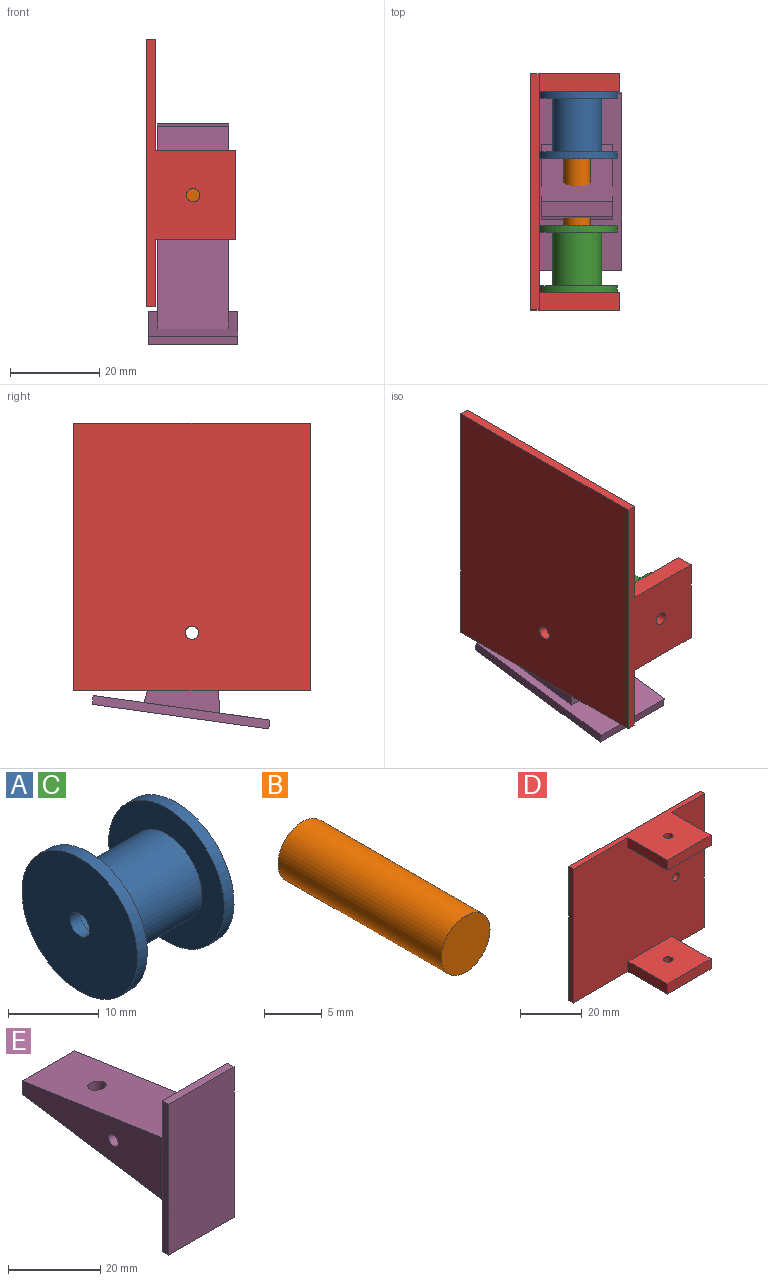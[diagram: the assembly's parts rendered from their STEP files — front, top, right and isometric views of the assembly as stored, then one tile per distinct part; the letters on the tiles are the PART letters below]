
ASSEMBLY  parts=5 mates=4
PART A: 10 faces, bbox 15x18x18 mm
  f0: plane 18x18mm, normal (-1,0,0), area 247.4mm2, adj f1,f9
  f1: cylinder r=1.5mm len=3mm, axis (-1,0,0), area 14.1mm2, adj f0,f2
  f2: plane 9x9mm, normal (1,0,0), area 56.5mm2, adj f1,f3
  f3: cylinder r=4.5mm len=13.5mm, axis (-1,0,0), area 381.7mm2, adj f2,f4
  f4: plane 18x18mm, normal (1,0,0), area 190.9mm2, adj f3,f5
  f5: cylinder r=9mm len=18mm, axis (-1,0,0), area 84.8mm2, adj f4,f6
  f6: plane 18x18mm, normal (-1,0,0), area 159.4mm2, adj f5,f7
  f7: cylinder r=5.5mm len=12mm, axis (-1,0,0), area 414.7mm2, adj f6,f8
  f8: plane 18x18mm, normal (1,0,0), area 159.4mm2, adj f7,f9
  f9: cylinder r=9mm len=18mm, axis (-1,0,0), area 84.8mm2, adj f0,f8
PART B: 3 faces, bbox 6x20x6 mm
  f0: cylinder r=3mm len=20mm, axis (0,1,0), area 377mm2, adj f1,f2
  f1: plane 6x6mm, normal (0,-1,0), area 28.3mm2, adj f0
  f2: plane 6x6mm, normal (0,1,0), area 28.3mm2, adj f0
PART C: same geometry as A
PART D: 17 faces, bbox 60x20x53 mm
  f0: plane 60x53mm, normal (0,-1,0), area 3012.9mm2, adj f1,f2,f3,f4,f6,f7,f8,f9
  f1: plane 60x20mm, normal (0,0,-1), area 472.9mm2, adj f0,f2,f4,f5,f12,f13,f14,f15
  f2: plane 53x2mm, normal (1,0,0), area 106mm2, adj f0,f1,f3,f5
  f3: plane 60x20mm, normal (0,0,1), area 472.9mm2, adj f0,f2,f4,f5,f7,f9,f10,f16
  f4: plane 53x2mm, normal (-1,0,0), area 106mm2, adj f0,f1,f3,f5
  f5: plane 60x53mm, normal (0,1,0), area 3172.9mm2, adj f1,f2,f3,f4,f6
  f6: cylinder r=1.5mm len=3mm, axis (0,-1,0), area 18.8mm2, adj f0,f5
  f7: plane 18x4mm, normal (-1,0,0), area 72mm2, adj f0,f3,f8,f10
  f8: plane 20x18mm, normal (0,0,-1), area 352.9mm2, adj f0,f7,f9,f10,f16
  f9: plane 18x4mm, normal (1,0,0), area 72mm2, adj f0,f3,f8,f10
  f10: plane 20x4mm, normal (0,-1,0), area 80mm2, adj f3,f7,f8,f9
  f11: plane 20x18mm, normal (0,0,1), area 352.9mm2, adj f0,f12,f13,f14,f15
  f12: plane 18x4mm, normal (-1,0,0), area 72mm2, adj f0,f1,f11,f14
  f13: plane 18x4mm, normal (1,0,0), area 72mm2, adj f0,f1,f11,f14
  f14: plane 20x4mm, normal (0,-1,0), area 80mm2, adj f1,f11,f12,f13
  f15: cylinder r=1.5mm len=4mm, axis (0,0,1), area 37.7mm2, adj f1,f11
  f16: cylinder r=1.5mm len=4mm, axis (0,0,1), area 37.7mm2, adj f3,f8
PART E: 13 faces, bbox 20.1x47.1x40.1 mm
  f0: plane 40x20mm, normal (0,1,0), area 528mm2, adj f1,f2,f3,f4,f6,f8,f9,f10
  f1: plane 20x2mm, normal (0,0,-1), area 40mm2, adj f0,f2,f4,f5
  f2: plane 40x2mm, normal (1,0,0), area 80mm2, adj f0,f1,f3,f5
  f3: plane 20x2mm, normal (0,0,1), area 40mm2, adj f0,f2,f4,f5
  f4: plane 40x2mm, normal (-1,0,0), area 80mm2, adj f0,f1,f3,f5
  f5: plane 40x20mm, normal (0,-1,0), area 800mm2, adj f1,f2,f3,f4
  f6: plane 45x16mm, normal (0,0.15,-0.99), area 715.3mm2, adj f0,f7,f9,f10,f12
  f7: plane 16x3.55mm, normal (0,1,0), area 56.8mm2, adj f6,f8,f9,f10
  f8: plane 45.13x16.13mm, normal (0,0.15,0.99), area 715.3mm2, adj f0,f7,f9,f10,f12
  f9: plane 45x17mm, normal (1,0,0), area 455.3mm2, adj f0,f6,f7,f8,f11
  f10: plane 45x17mm, normal (-1,0,0), area 455.3mm2, adj f0,f6,f7,f8,f11
  f11: cylinder r=1.5mm len=16mm, axis (-1,0,0), area 150.8mm2, adj f9,f10
  f12: cylinder r=2mm len=8.63mm, axis (0,0,-1), area 100.9mm2, adj f6,f8
PLACE A rot(axis=(0.71,-0.71,0),180deg) t=(-4.45,76.44,-45.22)mm
PLACE B rot(axis=(1,0,0),7.9deg) t=(-4.45,62.06,-42.97)mm
PLACE C rot(axis=(0.71,0.71,0),180deg) t=(-4.45,31.44,-45.22)mm
PLACE D rot(axis=(-0.58,0.58,0.58),120deg) t=(-14.95,53.94,-40.22)mm fixed
PLACE E rot(axis=(1,0,0),97.9deg) t=(-4.45,56.28,-74.06)mm
MATE fastened E.f12 <-> B.f0  axis (0,0.99,0.14) through (-4.45,52.15,-44.34)mm
MATE revolute D.f6 <-> E.f11  axis (1,0,0) through (-12.95,53.94,-57.22)mm
MATE fastened C.f1 <-> D.f15  axis (0,-1,0) through (-4.45,31.44,-45.22)mm
MATE fastened A.f1 <-> D.f15  axis (0,1,0) through (-4.45,76.44,-45.22)mm
